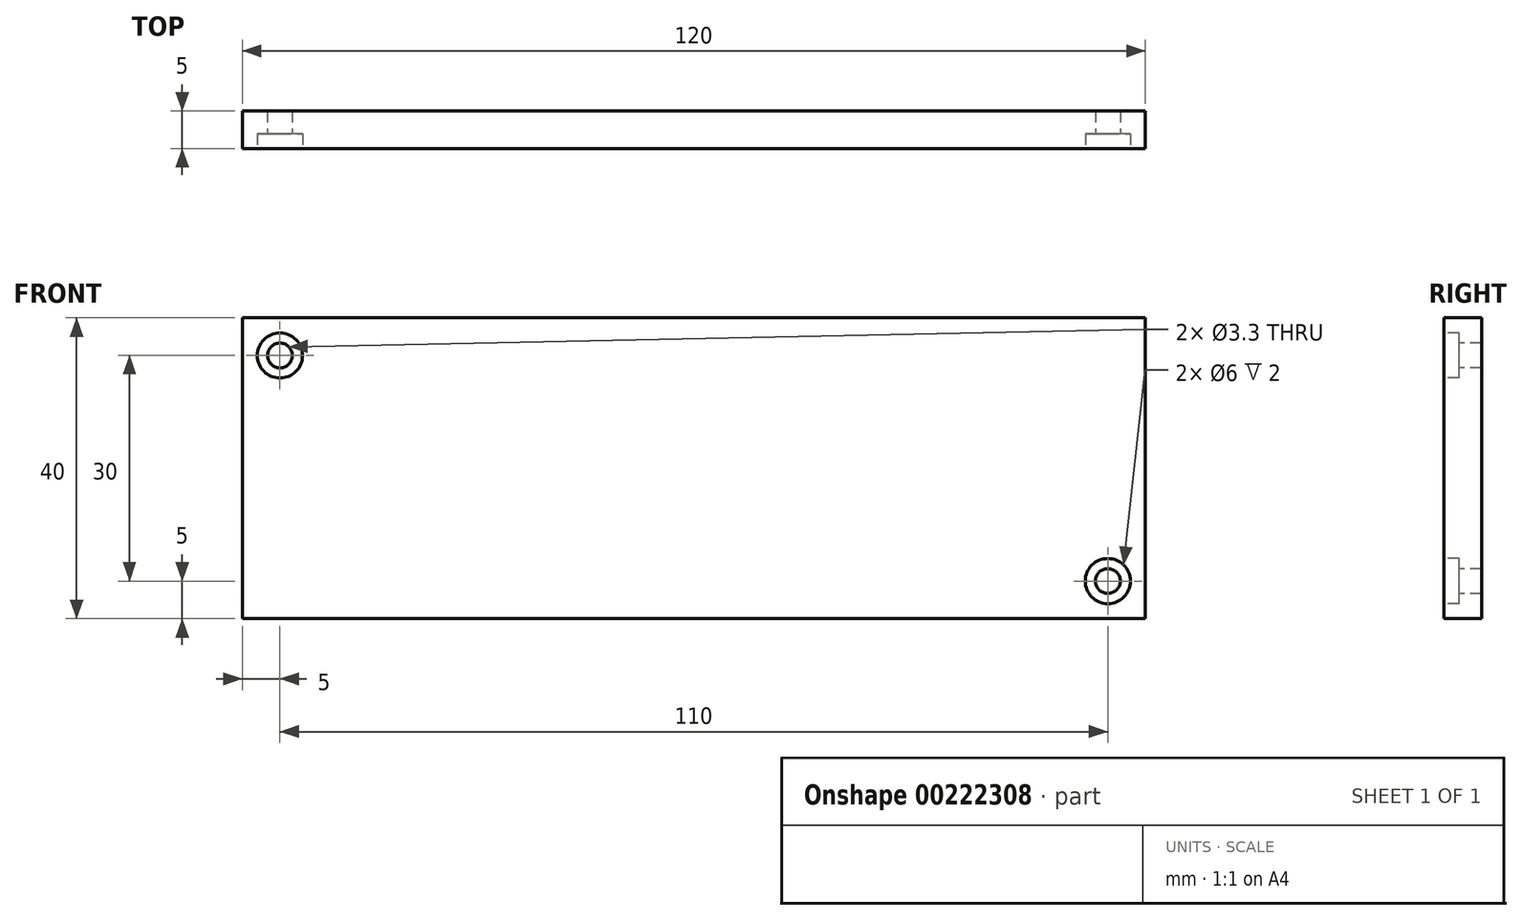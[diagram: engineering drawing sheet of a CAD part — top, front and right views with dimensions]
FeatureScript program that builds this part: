
annotation { "Feature Type Name" : "Feature", "Feature Type Description" : "" }
export const myFeature = defineFeature(function(context is Context, id is Id, definition is map)
    precondition{}
    {
        {
            var Q0;
            Q0=qCreatedBy(makeId("Front.planeOp"),FACE);
            var sketch = newSketch(context, id + "F0", { "sketchPlane" : qUnion([Q0])});
            skLineSegment(sketch, "E0.bottom", {"start": v(60, -20) * mm, "end": v(-60, -20) * mm});
            skLineSegment(sketch, "E0.top", {"start": v(60, 20) * mm, "end": v(-60, 20) * mm});
            skLineSegment(sketch, "E0.left", {"start": v(60, -20) * mm, "end": v(60, 20) * mm});
            skLineSegment(sketch, "E0.right", {"start": v(-60, -20) * mm, "end": v(-60, 20) * mm});
            skPoint(sketch, "E0.middle", {"position": v(0, 0) * mm});
            skSolve(sketch);
        }
        {
            var Q0;
            Q0=makeQuery(id+"F0.imprint","IMPRINT",FACE,{"disambiguationData":[TD([[makeQuery(id+"F0.imprint","IMPRINT",EDGE,{"derivedFrom":sQuery(id+"F0.wireOp",EDGE,"E0.bottom")}),-1.0]])]});
            extrude(context, id + "F1", {"entities" : qUnion([Q0]), "depth" : 5 * mm});
        }
        {
            var Q0;
            Q0=makeQuery(id+"F1.opExtrude","CAP_FACE",FACE,{"disambiguationData":[OSD([sQuery(id+"F0.wireOp",EDGE,"E0.bottom"),sQuery(id+"F0.wireOp",EDGE,"E0.top"),sQuery(id+"F0.wireOp",EDGE,"E0.left"),sQuery(id+"F0.wireOp",EDGE,"E0.right")])],"isStart":false});
            var sketch = newSketch(context, id + "F2", { "sketchPlane" : qUnion([Q0])});
            skPoint(sketch, "E1", {"position": v(-55, 15) * mm});
            skPoint(sketch, "E2", {"position": v(55, -15) * mm});
            skSolve(sketch);
        }
        {
            var Q0;
            Q0=sQuery(id+"F2.wireOp",VERTEX,"E1");
            var Q1;
            Q1=sQuery(id+"F2.wireOp",VERTEX,"E2");
            var Q2;
            Q2=makeQuery(id+"F1.opExtrude","SWEPT_BODY",BODY,{"disambiguationData":[OSD([sQuery(id+"F0.wireOp",EDGE,"E0.bottom"),sQuery(id+"F0.wireOp",EDGE,"E0.top"),sQuery(id+"F0.wireOp",EDGE,"E0.left"),sQuery(id+"F0.wireOp",EDGE,"E0.right")])]});
            hole(context, id + "F3", {"style" : HoleStyle.C_BORE, "endStyle" : HoleEndStyle.THROUGH, "holeDiameter" : 3.3 * mm, "cBoreDiameter" : 6 * mm, "cBoreDepth" : 2 * mm, "locations" : qUnion([Q0, Q1]), "scope" : qUnion([Q2]), "isTappedThrough" : true});
        }
    });
